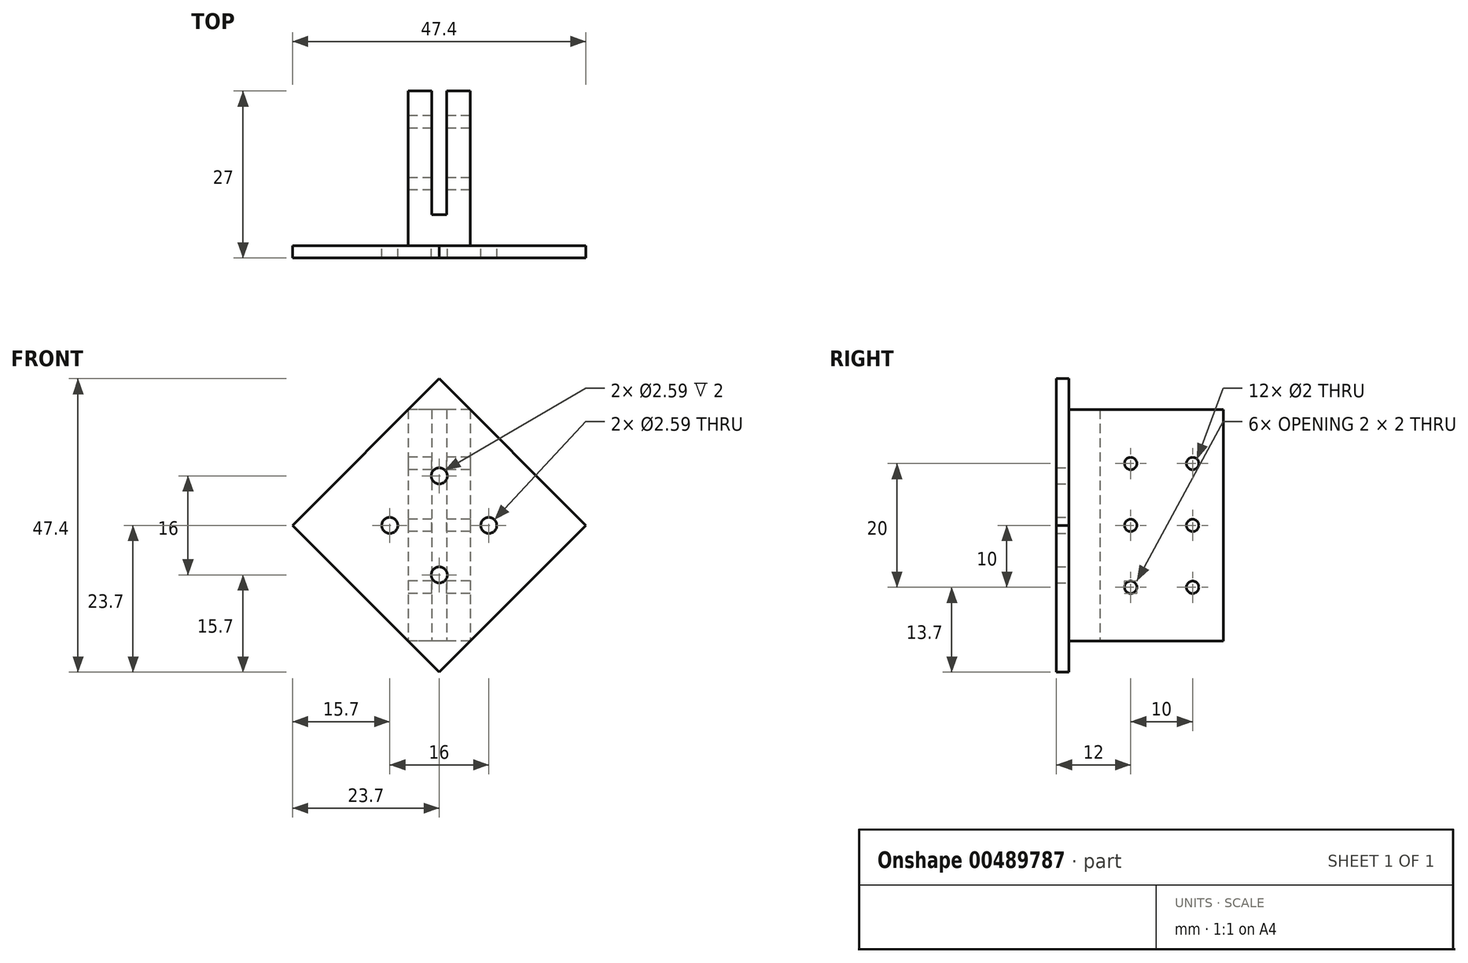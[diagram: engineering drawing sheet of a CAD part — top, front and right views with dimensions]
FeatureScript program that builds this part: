
annotation { "Feature Type Name" : "Feature", "Feature Type Description" : "" }
export const myFeature = defineFeature(function(context is Context, id is Id, definition is map)
    precondition{}
    {
        {
            var Q0;
            Q0=qCreatedBy(makeId("Front.planeOp"),FACE);
            var sketch = newSketch(context, id + "F0", { "sketchPlane" : qUnion([Q0])});
            skLineSegment(sketch, "E0.bottom", {"start": v(-27.5, 27.5) * mm, "end": v(27.5, 27.5) * mm});
            skLineSegment(sketch, "E0.top", {"start": v(-27.5, -27.5) * mm, "end": v(27.5, -27.5) * mm});
            skLineSegment(sketch, "E0.left", {"start": v(-27.5, 27.5) * mm, "end": v(-27.5, -27.5) * mm});
            skLineSegment(sketch, "E0.right", {"start": v(27.5, 27.5) * mm, "end": v(27.5, -27.5) * mm});
            skCircle(sketch, "E1", {"center": v(-8, 0) * mm, "radius": 1.3 * mm});
            skLineSegment(sketch, "E2", {"start": v(5.69, 29.4) * mm, "end": v(-11.28, 46.36) * mm});
            skLineSegment(sketch, "E3", {"start": v(-11.28, 46.36) * mm, "end": v(-46.6, 11.04) * mm});
            skLineSegment(sketch, "E4", {"start": v(-46.6, 11.04) * mm, "end": v(-29.63, -5.93) * mm});
            skLineSegment(sketch, "E5", {"start": v(-29.63, -5.93) * mm, "end": v(5.69, 29.4) * mm});
            skCircle(sketch, "E6.1.0", {"center": v(0, -8) * mm, "radius": 1.3 * mm});
            skLineSegment(sketch, "E6.1.1", {"start": v(5.93, -29.63) * mm, "end": v(-29.4, 5.69) * mm});
            skLineSegment(sketch, "E6.1.2", {"start": v(-11.04, -46.6) * mm, "end": v(5.93, -29.63) * mm});
            skLineSegment(sketch, "E6.1.3", {"start": v(-46.36, -11.28) * mm, "end": v(-11.04, -46.6) * mm});
            skLineSegment(sketch, "E6.1.4", {"start": v(-29.4, 5.69) * mm, "end": v(-46.36, -11.28) * mm});
            skCircle(sketch, "E6.2.0", {"center": v(8, 0) * mm, "radius": 1.3 * mm});
            skLineSegment(sketch, "E6.2.1", {"start": v(29.63, 5.93) * mm, "end": v(-5.69, -29.4) * mm});
            skLineSegment(sketch, "E6.2.2", {"start": v(46.6, -11.04) * mm, "end": v(29.63, 5.93) * mm});
            skLineSegment(sketch, "E6.2.3", {"start": v(11.28, -46.36) * mm, "end": v(46.6, -11.04) * mm});
            skLineSegment(sketch, "E6.2.4", {"start": v(-5.69, -29.4) * mm, "end": v(11.28, -46.36) * mm});
            skCircle(sketch, "E6.3.0", {"center": v(0, 8) * mm, "radius": 1.3 * mm});
            skLineSegment(sketch, "E6.3.1", {"start": v(-5.93, 29.63) * mm, "end": v(29.4, -5.69) * mm});
            skLineSegment(sketch, "E6.3.2", {"start": v(11.04, 46.6) * mm, "end": v(-5.93, 29.63) * mm});
            skLineSegment(sketch, "E6.3.3", {"start": v(46.36, 11.28) * mm, "end": v(11.04, 46.6) * mm});
            skLineSegment(sketch, "E6.3.4", {"start": v(29.4, -5.69) * mm, "end": v(46.36, 11.28) * mm});
            skPoint(sketch, "E6.center", {"position": v(0, 0) * mm});
            skSolve(sketch);
        }
        {
            var Q0;
            Q0=makeQuery(id+"F0.imprint","IMPRINT",FACE,{"disambiguationData":[TD([[makeQuery(id+"F0.imprint","IMPRINT",EDGE,{"derivedFrom":sQuery(id+"F0.wireOp",EDGE,"E1")}),-1.0]])]});
            extrude(context, id + "F1", {"entities" : qUnion([Q0]), "depth" : 2 * mm});
        }
        {
            var Q0;
            Q0=makeQuery(id+"F1.opExtrude","CAP_FACE",FACE,{"disambiguationData":[OSD([sQuery(id+"F0.wireOp",EDGE,"E1"),sQuery(id+"F0.wireOp",EDGE,"E5"),sQuery(id+"F0.wireOp",EDGE,"E6.1.0"),sQuery(id+"F0.wireOp",EDGE,"E6.1.1"),sQuery(id+"F0.wireOp",EDGE,"E6.2.0"),sQuery(id+"F0.wireOp",EDGE,"E6.2.1"),sQuery(id+"F0.wireOp",EDGE,"E6.3.0"),sQuery(id+"F0.wireOp",EDGE,"E6.3.1")])],"isStart":true});
            var sketch = newSketch(context, id + "F2", { "sketchPlane" : qUnion([Q0])});
            skLineSegment(sketch, "E7.bottom", {"start": v(-5, 18.7) * mm, "end": v(5, 18.7) * mm});
            skLineSegment(sketch, "E7.top", {"start": v(-5, -18.7) * mm, "end": v(5, -18.7) * mm});
            skLineSegment(sketch, "E7.left", {"start": v(-5, 18.7) * mm, "end": v(-5, -18.7) * mm});
            skLineSegment(sketch, "E7.right", {"start": v(5, 18.7) * mm, "end": v(5, -18.7) * mm});
            skSolve(sketch);
        }
        {
            var Q0;
            Q0=qSketchRegion(id+"F2",true);
            extrude(context, id + "F3", {"entities" : qUnion([Q0]), "operationType" : NewBodyOperationType.ADD, "depth" : 25 * mm});
        }
        {
            var Q0;
            Q0=makeQuery(id+"F3.opExtrude","CAP_FACE",FACE,{"disambiguationData":[OSD([sQuery(id+"F2.wireOp",EDGE,"E7.bottom"),sQuery(id+"F2.wireOp",EDGE,"E7.top"),sQuery(id+"F2.wireOp",EDGE,"E7.left"),sQuery(id+"F2.wireOp",EDGE,"E7.right")])],"isStart":false});
            var sketch = newSketch(context, id + "F4", { "sketchPlane" : qUnion([Q0])});
            skLineSegment(sketch, "E8.bottom", {"start": v(-1.2, 18.7) * mm, "end": v(1.2, 18.7) * mm});
            skLineSegment(sketch, "E8.top", {"start": v(-1.2, -18.7) * mm, "end": v(1.2, -18.7) * mm});
            skLineSegment(sketch, "E8.left", {"start": v(-1.2, 18.7) * mm, "end": v(-1.2, -18.7) * mm});
            skLineSegment(sketch, "E8.right", {"start": v(1.2, 18.7) * mm, "end": v(1.2, -18.7) * mm});
            skSolve(sketch);
        }
        {
            var Q0;
            Q0=qSketchRegion(id+"F4",true);
            extrude(context, id + "F5", {"entities" : qUnion([Q0]), "operationType" : NewBodyOperationType.REMOVE, "oppositeDirection" : true, "depth" : 20 * mm});
        }
        {
            var Q0;
            Q0=makeQuery(id+"F3.opExtrude","SWEPT_FACE",FACE,{"disambiguationData":[OSD([sQuery(id+"F2.wireOp",EDGE,"E7.right")])]});
            var sketch = newSketch(context, id + "F6", { "sketchPlane" : qUnion([Q0])});
            skCircle(sketch, "E9", {"center": v(-20, 10) * mm, "radius": 1 * mm});
            skCircle(sketch, "E10", {"center": v(-20, -10) * mm, "radius": 1 * mm});
            skCircle(sketch, "E11", {"center": v(-20, 0) * mm, "radius": 1 * mm});
            skCircle(sketch, "E12", {"center": v(-10, 0) * mm, "radius": 1 * mm});
            skCircle(sketch, "E13", {"center": v(-10, 10) * mm, "radius": 1 * mm});
            skCircle(sketch, "E14", {"center": v(-10, -10) * mm, "radius": 1 * mm});
            skSolve(sketch);
        }
        {
            var Q0;
            Q0=makeQuery(id+"F6.imprint","IMPRINT",FACE,{"disambiguationData":[TD([[makeQuery(id+"F6.imprint","IMPRINT",EDGE,{"derivedFrom":sQuery(id+"F6.wireOp",EDGE,"E9")}),1.0]])]});
            var Q1;
            Q1=makeQuery(id+"F6.imprint","IMPRINT",FACE,{"disambiguationData":[TD([[makeQuery(id+"F6.imprint","IMPRINT",EDGE,{"derivedFrom":sQuery(id+"F6.wireOp",EDGE,"E13")}),1.0]])]});
            var Q2;
            Q2=makeQuery(id+"F6.imprint","IMPRINT",FACE,{"disambiguationData":[TD([[makeQuery(id+"F6.imprint","IMPRINT",EDGE,{"derivedFrom":sQuery(id+"F6.wireOp",EDGE,"E12")}),1.0]])]});
            var Q3;
            Q3=makeQuery(id+"F6.imprint","IMPRINT",FACE,{"disambiguationData":[TD([[makeQuery(id+"F6.imprint","IMPRINT",EDGE,{"derivedFrom":sQuery(id+"F6.wireOp",EDGE,"E11")}),1.0]])]});
            var Q4;
            Q4=makeQuery(id+"F6.imprint","IMPRINT",FACE,{"disambiguationData":[TD([[makeQuery(id+"F6.imprint","IMPRINT",EDGE,{"derivedFrom":sQuery(id+"F6.wireOp",EDGE,"E10")}),1.0]])]});
            var Q5;
            Q5=makeQuery(id+"F6.imprint","IMPRINT",FACE,{"disambiguationData":[TD([[makeQuery(id+"F6.imprint","IMPRINT",EDGE,{"derivedFrom":sQuery(id+"F6.wireOp",EDGE,"E14")}),1.0]])]});
            extrude(context, id + "F7", {"entities" : qUnion([Q0, Q1, Q2, Q3, Q4, Q5]), "operationType" : NewBodyOperationType.REMOVE, "oppositeDirection" : true, "depth" : 25 * mm});
        }
    });
